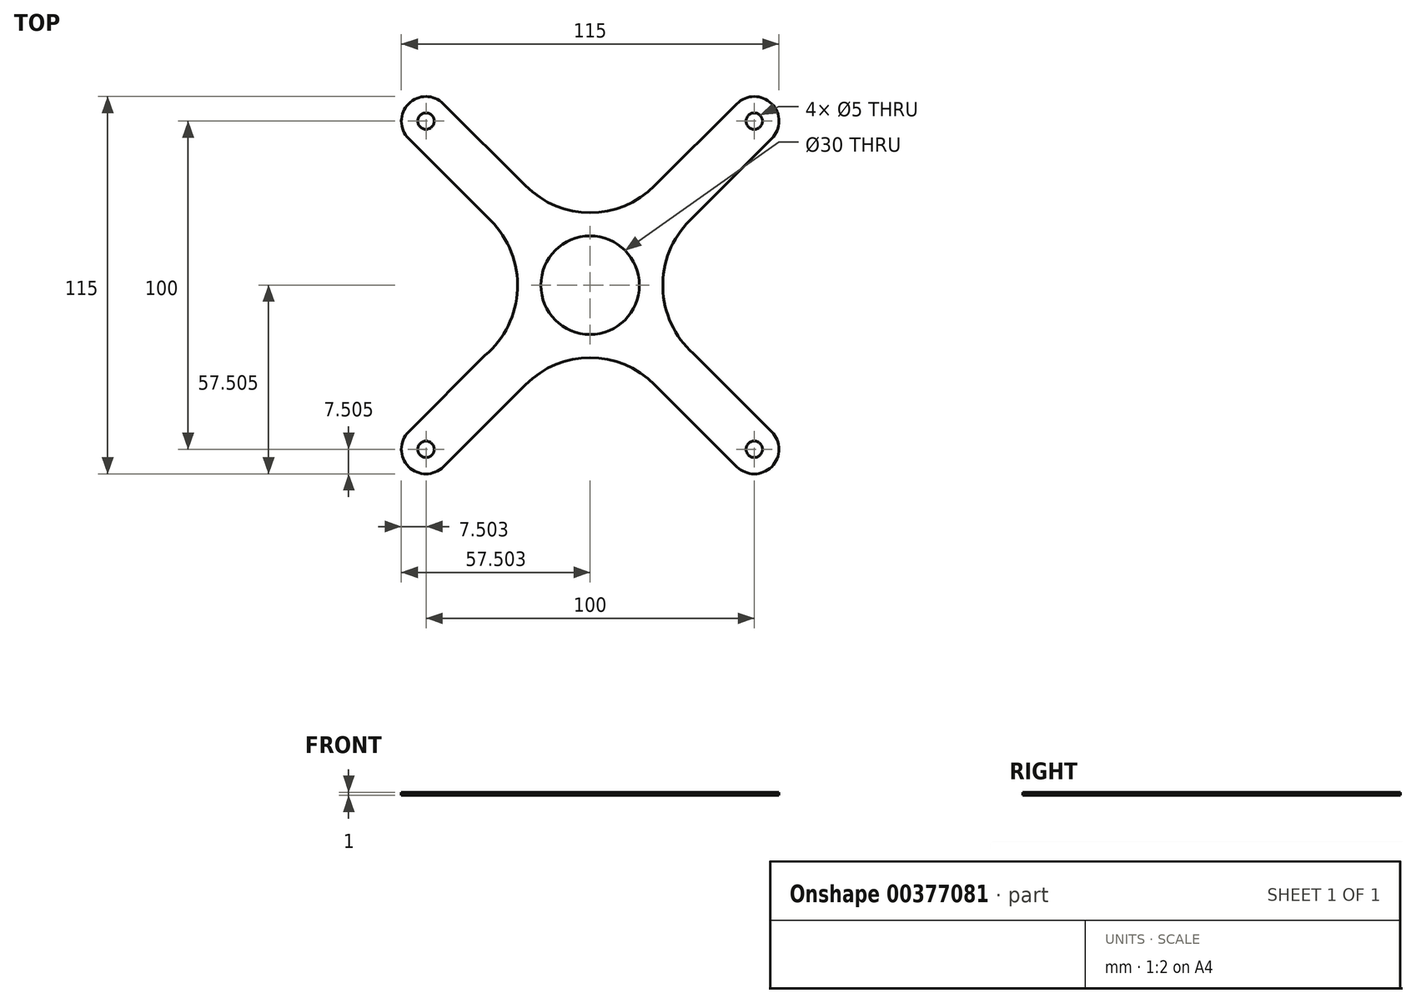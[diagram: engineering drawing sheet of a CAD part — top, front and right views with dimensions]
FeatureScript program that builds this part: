
annotation { "Feature Type Name" : "Feature", "Feature Type Description" : "" }
export const myFeature = defineFeature(function(context is Context, id is Id, definition is map)
    precondition{}
    {
        {
            var Q0;
            Q0=qCreatedBy(makeId("Top.planeOp"),FACE);
            var sketch = newSketch(context, id + "F0", { "sketchPlane" : qUnion([Q0])});
            skCircle(sketch, "E0", {"center": v(-58.44, 41.74) * mm, "radius": 2.5 * mm});
            skCircle(sketch, "E1", {"center": v(41.56, 41.74) * mm, "radius": 2.5 * mm});
            skCircle(sketch, "E2", {"center": v(41.56, -58.26) * mm, "radius": 2.5 * mm});
            skCircle(sketch, "E3", {"center": v(-58.44, -58.26) * mm, "radius": 2.5 * mm});
            skArc(sketch, "E4", {"start": v(-49.6, 50.58) * mm, "mid": v(-67.28, 50.58) * mm, "end": v(-67.28, 32.9) * mm});
            skArc(sketch, "E5", {"start": v(50.4, 32.9) * mm, "mid": v(50.4, 50.58) * mm, "end": v(32.72, 50.58) * mm});
            skArc(sketch, "E6", {"start": v(-67.28, -49.42) * mm, "mid": v(-67.28, -67.1) * mm, "end": v(-49.6, -67.1) * mm});
            skArc(sketch, "E7", {"start": v(32.72, -67.1) * mm, "mid": v(50.4, -67.1) * mm, "end": v(50.4, -49.42) * mm});
            skLineSegment(sketch, "E8.0", {"start": v(-24.6, 25.58) * mm, "end": v(-49.6, 50.58) * mm});
            skLineSegment(sketch, "E9.0", {"start": v(-42.28, 7.9) * mm, "end": v(-67.28, 32.9) * mm});
            skLineSegment(sketch, "E10.0", {"start": v(-42.28, -24.42) * mm, "end": v(-67.28, -49.42) * mm});
            skLineSegment(sketch, "E11.0", {"start": v(-24.6, -42.1) * mm, "end": v(-49.6, -67.1) * mm});
            skLineSegment(sketch, "E12.0", {"start": v(50.4, -49.42) * mm, "end": v(25.4, -24.42) * mm});
            skLineSegment(sketch, "E13.0", {"start": v(32.72, -67.1) * mm, "end": v(7.72, -42.1) * mm});
            skLineSegment(sketch, "E14.0", {"start": v(25.4, 7.9) * mm, "end": v(50.4, 32.9) * mm});
            skLineSegment(sketch, "E15.0", {"start": v(7.72, 25.58) * mm, "end": v(32.72, 50.58) * mm});
            skArc(sketch, "E16", {"start": v(-42.28, 7.9) * mm, "mid": v(-35.58, -9.36) * mm, "end": v(-43.8, -25.95) * mm});
            skArc(sketch, "E17", {"start": v(-24.6, 25.58) * mm, "mid": v(-8.44, 18.89) * mm, "end": v(7.72, 25.58) * mm});
            skArc(sketch, "E18", {"start": v(25.4, 7.9) * mm, "mid": v(18.7, -8.97) * mm, "end": v(26.4, -25.42) * mm});
            skArc(sketch, "E19", {"start": v(7.72, -42.1) * mm, "mid": v(-8.44, -35.4) * mm, "end": v(-24.6, -42.1) * mm});
            skLineSegment(sketch, "E20.0", {"start": v(-28.13, 22.05) * mm, "end": v(-53.13, 47.05) * mm});
            skArc(sketch, "E21.0", {"start": v(-53.13, 47.05) * mm, "mid": v(-63.74, 47.05) * mm, "end": v(-63.74, 36.44) * mm});
            skLineSegment(sketch, "E22.0", {"start": v(-38.74, 11.44) * mm, "end": v(-63.74, 36.44) * mm});
            skArc(sketch, "E23.0", {"start": v(-38.74, 11.44) * mm, "mid": v(-30.58, -9.59) * mm, "end": v(-40.6, -29.8) * mm});
            skLineSegment(sketch, "E24.0", {"start": v(-38.74, -27.95) * mm, "end": v(-63.74, -52.95) * mm});
            skArc(sketch, "E25.0", {"start": v(-63.74, -52.95) * mm, "mid": v(-63.74, -63.56) * mm, "end": v(-53.13, -63.56) * mm});
            skLineSegment(sketch, "E26.0", {"start": v(-28.13, -38.56) * mm, "end": v(-53.13, -63.56) * mm});
            skArc(sketch, "E27.0", {"start": v(11.26, -38.56) * mm, "mid": v(-8.44, -30.4) * mm, "end": v(-28.13, -38.56) * mm});
            skLineSegment(sketch, "E28.0", {"start": v(36.26, -63.56) * mm, "end": v(11.26, -38.56) * mm});
            skArc(sketch, "E29.0", {"start": v(36.26, -63.56) * mm, "mid": v(46.87, -63.56) * mm, "end": v(46.87, -52.95) * mm});
            skLineSegment(sketch, "E30.0", {"start": v(46.87, -52.95) * mm, "end": v(21.87, -27.95) * mm});
            skArc(sketch, "E31.0", {"start": v(21.87, 11.44) * mm, "mid": v(13.7, -9.12) * mm, "end": v(23.09, -29.16) * mm});
            skLineSegment(sketch, "E32.0", {"start": v(21.87, 11.44) * mm, "end": v(46.87, 36.44) * mm});
            skArc(sketch, "E33.0", {"start": v(46.87, 36.44) * mm, "mid": v(46.87, 47.05) * mm, "end": v(36.26, 47.05) * mm});
            skLineSegment(sketch, "E34.0", {"start": v(11.26, 22.05) * mm, "end": v(36.26, 47.05) * mm});
            skArc(sketch, "E35.0", {"start": v(-28.13, 22.05) * mm, "mid": v(-8.44, 13.89) * mm, "end": v(11.26, 22.05) * mm});
            skCircle(sketch, "E36", {"center": v(-8.44, -8.26) * mm, "radius": 15 * mm});
            skSolve(sketch);
        }
        {
            var Q0;
            Q0=makeQuery(id+"F0.imprint","IMPRINT",FACE,{"disambiguationData":[TD([[makeQuery(id+"F0.imprint","IMPRINT",EDGE,{"derivedFrom":sQuery(id+"F0.wireOp",EDGE,"E0")}),-1.0]])]});
            extrude(context, id + "F1", {"entities" : qUnion([Q0]), "depth" : 1 * mm});
        }
    });
